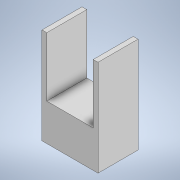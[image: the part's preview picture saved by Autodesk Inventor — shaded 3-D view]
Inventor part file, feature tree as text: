
AUTODESK INVENTOR PART (.ipt)
format: ipt  version: 2020 (Build 240168000, 168)  size: 120,832 bytes
history: native  units: mm
features: extrude x2, sketch x2
ambient origin geometry x8: Origin, YZ Plane, XZ Plane, XY Plane, X Axis, Y Axis, Z Axis, Center Point
bodies: Solid1 (feature_tree)
feature tree (4):
  extrude  "Extrusion1"  Depth=80.0mm
  extrude  "Extrusion2"  Depth=6.0mm
  sketch  "Sketch1"  dims[d0=70.0mm d1=80.0mm]
  sketch  "Sketch2"  dims[d2=80.0mm d3=6.0mm d4=50.0mm d5=0.0mm d7=6.0mm d8=40.0mm d9=0.0mm d6=0.5mm]
